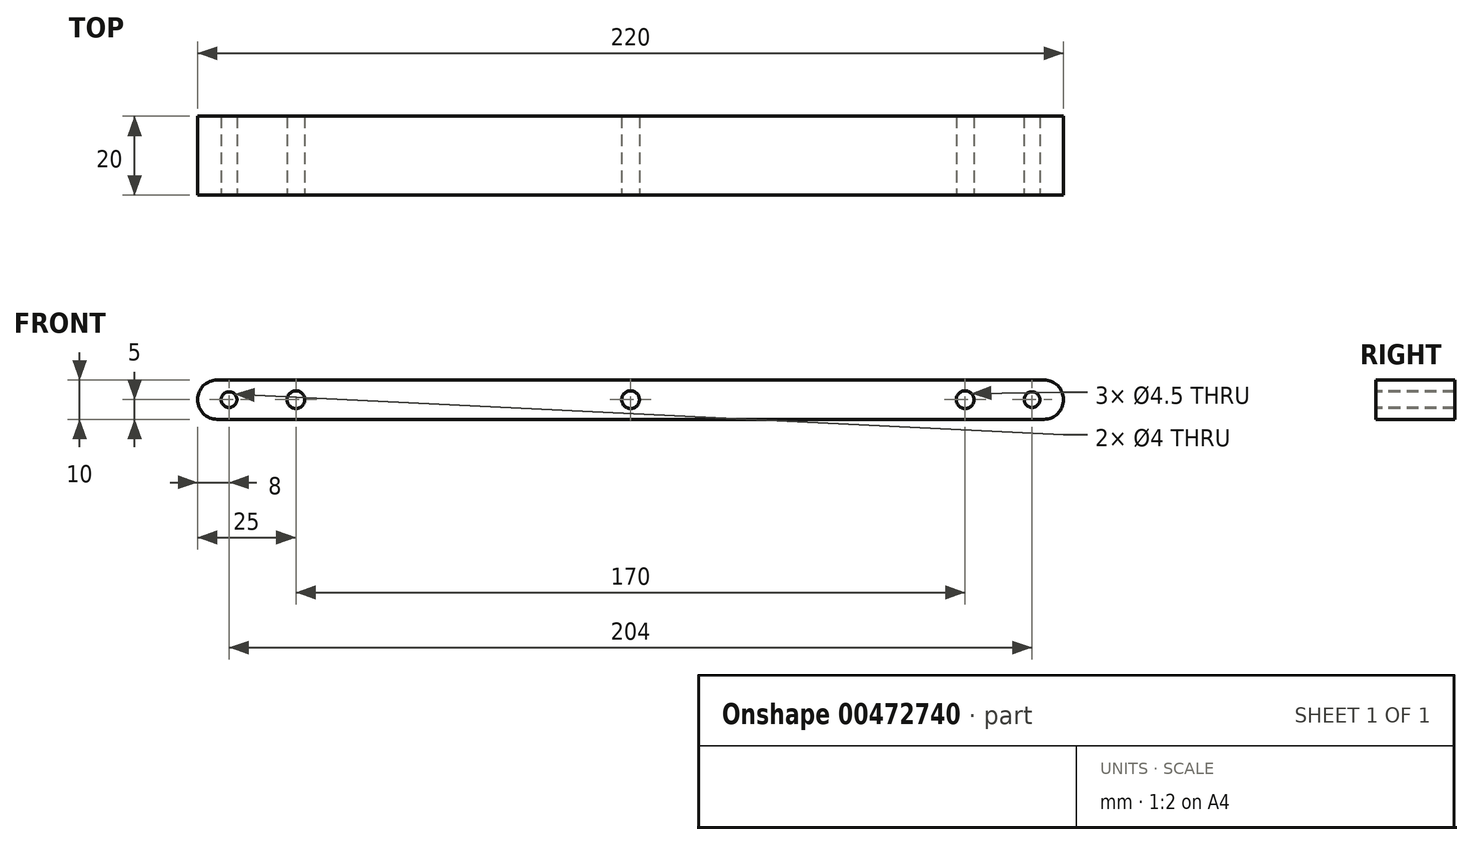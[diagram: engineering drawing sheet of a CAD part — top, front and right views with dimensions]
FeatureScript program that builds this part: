
annotation { "Feature Type Name" : "Feature", "Feature Type Description" : "" }
export const myFeature = defineFeature(function(context is Context, id is Id, definition is map)
    precondition{}
    {
        {
            var Q0;
            Q0=qCreatedBy(makeId("Front.planeOp"),FACE);
            var sketch = newSketch(context, id + "F0", { "sketchPlane" : qUnion([Q0])});
            skArc(sketch, "E0", {"start": v(0, -5) * mm, "mid": v(5, 0) * mm, "end": v(0, 5) * mm});
            skArc(sketch, "E1", {"start": v(-210, 5) * mm, "mid": v(-215, 0) * mm, "end": v(-210, -5) * mm});
            skLineSegment(sketch, "E2", {"start": v(0, 5) * mm, "end": v(-210, 5) * mm});
            skLineSegment(sketch, "E3", {"start": v(-210, 0) * mm, "end": v(0, 0) * mm, "construction": true});
            skLineSegment(sketch, "E4.MirrorCS", {"start": v(0, -5) * mm, "end": v(-210, -5) * mm});
            skSolve(sketch);
        }
        {
            var Q0;
            Q0 = qSketchRegion(id + "F0", true);
            extrude(context, id + "F1", {"entities" : qUnion([Q0]), "depth" : 20 * mm, "offsetDistance" : 25 * mm});
        }
        {
            var Q0;
            Q0=makeQuery(id+"F1.opExtrude","CAP_FACE",FACE,{"disambiguationData":[OSD([sQuery(id+"F0.wireOp",EDGE,"E0"),sQuery(id+"F0.wireOp",EDGE,"E1"),sQuery(id+"F0.wireOp",EDGE,"E2"),sQuery(id+"F0.wireOp",EDGE,"E4.MirrorCS")])],"isStart":false});
            var sketch = newSketch(context, id + "F2", { "sketchPlane" : qUnion([Q0])});
            skLineSegment(sketch, "E5", {"start": v(-215, 0) * mm, "end": v(5, 0) * mm, "construction": true});
            skCircle(sketch, "E6", {"center": v(-190, 0) * mm, "radius": 2.25 * mm});
            skCircle(sketch, "E7", {"center": v(-20, 0) * mm, "radius": 2.25 * mm});
            skLineSegment(sketch, "E8", {"start": v(-105, 5) * mm, "end": v(-105, -5) * mm, "construction": true});
            skCircle(sketch, "E9", {"center": v(-105, 0) * mm, "radius": 2.25 * mm});
            skCircle(sketch, "E10", {"center": v(-207, 0) * mm, "radius": 2 * mm});
            skCircle(sketch, "E11", {"center": v(-3, 0) * mm, "radius": 2 * mm});
            skSolve(sketch);
        }
        {
            var Q0;
            Q0 = qSketchRegion(id + "F2", true);
            extrude(context, id + "F3", {"entities" : qUnion([Q0]), "operationType" : NewBodyOperationType.REMOVE, "endBound" : BoundingType.THROUGH_ALL, "oppositeDirection" : true, "depth" : 25 * mm, "offsetDistance" : 25 * mm});
        }
    });
